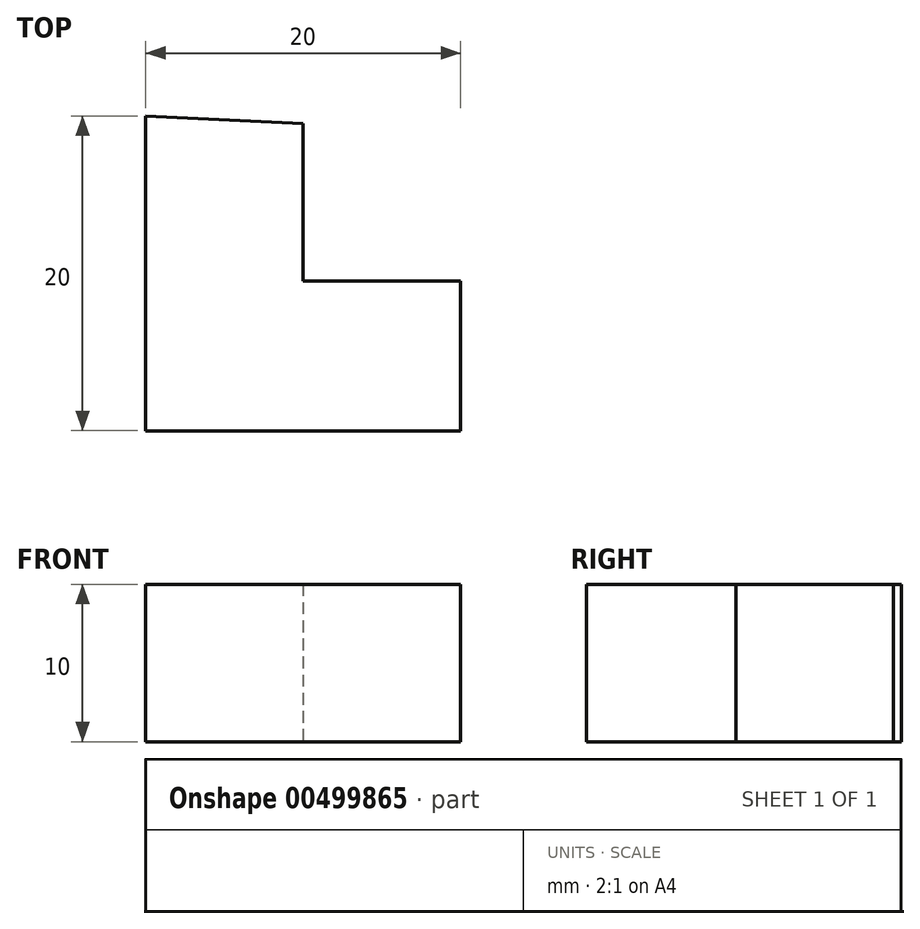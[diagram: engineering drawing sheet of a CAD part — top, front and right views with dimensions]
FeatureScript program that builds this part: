
annotation { "Feature Type Name" : "Feature", "Feature Type Description" : "" }
export const myFeature = defineFeature(function(context is Context, id is Id, definition is map)
    precondition{}
    {
        {
            var Q0;
            Q0=qCreatedBy(makeId("Top.planeOp"),FACE);
            var sketch = newSketch(context, id + "F0", { "sketchPlane" : qUnion([Q0])});
            skLineSegment(sketch, "E0", {"start": v(-9.99, 10.5) * mm, "end": v(-9.99, -9.5) * mm});
            skLineSegment(sketch, "E1", {"start": v(-9.99, -9.5) * mm, "end": v(10.01, -9.5) * mm});
            skLineSegment(sketch, "E2", {"start": v(10.01, -9.5) * mm, "end": v(10.01, 0) * mm});
            skLineSegment(sketch, "E3", {"start": v(10.01, 0) * mm, "end": v(-0.78, 0) * mm});
            skLineSegment(sketch, "E4", {"start": v(0, 0) * mm, "end": v(0, 10) * mm});
            skLineSegment(sketch, "E5", {"start": v(0, 10) * mm, "end": v(-9.99, 10.5) * mm});
            skSolve(sketch);
        }
        {
            var Q0;
            Q0=makeQuery(id+"F0.imprint","IMPRINT",FACE,{"disambiguationData":[TD([[makeQuery(id+"F0.imprint","IMPRINT",EDGE,{"derivedFrom":sQuery(id+"F0.wireOp",EDGE,"E0")}),1.0]])]});
            extrude(context, id + "F1", {"entities" : qUnion([Q0]), "depth" : 10 * mm});
        }
    });
